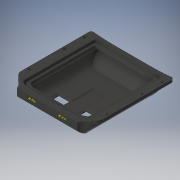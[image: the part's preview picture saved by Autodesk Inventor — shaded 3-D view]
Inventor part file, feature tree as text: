
AUTODESK INVENTOR PART (.ipt)
format: ipt  version: 2019.2 (Build 232265000, 265)  size: 4,940,800 bytes
history: native  units: mm
features: extrude x13, sketch x11, other x10, fillet x7, chamfer x6, plane x3, loft x2, shell x1, emboss x1, projected_geometry x1
ambient origin geometry x8: Origin, YZ Plane, XZ Plane, XY Plane, X Axis, Y Axis, Z Axis, Center Point
bodies: Solid2 (feature_tree), Solid1 (feature_tree)
feature tree (55):
  other  "deck.ipt"
  extrude  "Extrusion1"  Depth=10.0mm
  chamfer  "Chamfer1"  Distance=170.0mm
  chamfer  "Chamfer2"  Distance=20.0mm Angle=45.0deg
  fillet  "Fillet1"  Radius=5.0mm
  fillet  "Fillet2"  Radius=4.0mm
  extrude  "Extrusion4"  Depth=5.0mm
  shell  "Shell1"  Thickness=5.0mm
  extrude  "Extrusion6"  Depth=10.0mm
  emboss  "Emboss1"
  fillet  "Fillet4"  Radius=200.0mm
  sketch  "Sketch8"  dims[d4=18.0mm]
  sketch  "Sketch9"  dims[d5=12.217305mm]
  plane  "Work Plane5"
  extrude  "Extrusion12"  Depth=0.5mm TaperAngle=0.0deg
  extrude  "Extrusion13"  Depth=10.0mm
  extrude  "Extrusion15"  Depth=10.0mm
  extrude  "Extrusion14"  Depth=10.0mm
  fillet  "Fillet8"  Radius=7.0mm
  fillet  "Fillet9"  Radius=15.0mm
  plane  "Work Plane6"
  sketch  "Sketch14"  dims[d6=12.0mm]
  extrude  "Extrusion18"  Depth=10.0mm
  fillet  "Fillet11"  Radius=0.5mm
  extrude  "Extrusion19"  Depth=10.0mm
  plane  "Work Plane7"
  sketch  "Sketch17"  dims[d30=20.0mm d31=30.0mm d32=45.0deg d33=4.0mm]
  sketch  "Sketch18"  dims[d34=186.25mm d35=0.0mm d37=5.0mm d48=5.0mm]
  loft  "Loft1"
  loft  "Loft2"
  other  "MOTOR1_3"
  other  "MOTOR1_2"
  other  "MOTOR1_1"
  other  "MOTOR2_3"
  other  "MOTOR2_2"
  other  "MOTOR2_1"
  sketch  "Sketch19"  dims[d49=20.0mm d51=40.0mm d52=10.0mm d54=10.0mm d56=20.0mm d58=70.0mm d59=10.0mm d61=10.0mm d63=200.0mm]
  extrude  "Extrusion20"  Depth=10.0mm
  extrude  "Extrusion25"  Depth=10.0mm
  chamfer  "Chamfer5"  Distance=6.0mm
  sketch  "Sketch20"  dims[d64=100.0mm d65=0.0mm d66=0.5mm d67=0.0mm]
  extrude  "Extrusion24"  Depth=10.0mm
  extrude  "Extrusion23"  [1 undecoded]
  chamfer  "Chamfer8"  Distance=10.0mm
  fillet  "Fillet14"  Radius=10.0mm
  chamfer  "Chamfer9"  Distance=10.0mm
  chamfer  "Chamfer10"  Distance=5.0mm
  other  "Solid6::deck.ipt"
  other  "TaggingFeature1"
  other  "Front Profile"
  sketch  "Sketch6"  dims[d0=10.0mm d2=82.0mm]
  sketch  "Sketch7"  dims[d3=35.0mm]
  projected_geometry  "Projected Loop2"
  sketch  "Sketch15"  dims[d7=45.0mm d8=170.0mm d9=0.0mm d26=20.0mm d27=30.0mm d28=45.0deg d29=5.0mm]
  sketch  "Sketch21"  dims[d68=5.0mm d69=18.0mm d70=77.400415mm d71=42.0mm d72=7.0mm d73=15.0mm d74=0.5mm d75=0.5mm d76=3.0mm d77=1.0mm d80=10.0mm d81=3.3mm d82=0.5mm d83=6.0mm d84=3.3mm d97=-25.0mm d98=10.0mm d99=10.0mm d100=10.0mm d101=5.0mm d102=13.0mm d103=0.0mm d104=7.0mm d105=7.0mm d106=7.0mm d108=7.0mm d109=4.0mm d110=4.0mm d111=4.0mm d114=10.0mm d115=0.0mm d116=0.0mm d117=0.0mm d118=8.0mm d119=0.0mm d123=0.0mm d124=4.0mm d125=3.0mm d137=-3.5mm d148=0.6mm d149=0.0mm d150=3.0mm d158=3.0mm d161=4.0mm d164=0.6mm d165=0.6mm d166=0.6mm d170=0.6mm d171=0.0mm d172=23.898481mm d173=23.898mm d174=10.0mm d175=5.5mm d177=30.0mm d180=5.5mm d181=5.5mm d182=2.75mm d183=2.75mm d184=2.75mm d185=2.75mm d186=10.0mm d187=10.0mm d194=0.0mm d195=90.0deg d196=0.6mm d197=0.59953mm d198=0.6mm d199=0.6mm d200=0.6mm d201=0.6mm d202=0.6mm d203=-19.0mm d204=0.0mm d205=90.0deg d206=0.0mm d207=90.0deg d208=0.0mm d209=90.0deg d210=9.0mm d211=9.0mm d212=3.0mm d215=5.0mm d216=5.0mm d217=5.0mm d222=1.5mm d223=0.0mm d224=1.0mm d225=2.0mm d226=45.0deg d238=25.0mm d240=12.0mm d241=10.0mm d242=0.0mm d243=2.0mm d244=1.0mm d245=45.0deg d249=25.0mm d250=25.0mm d251=5.0mm d252=2.5mm d253=0.0mm d254=1.0mm d255=1.0mm d256=1.0mm d257=1.0mm d258=3.0mm d259=0.0mm d260=10.0mm d261=6.0mm d262=2.5mm d263=45.0deg d264=6.0mm d265=2.5mm d266=45.0deg]
note: 1 required parameter value undecoded (feature->parameter linkage not recoverable at this tier; creation-order binding heuristic only, values carry confidence <= 0.55)
